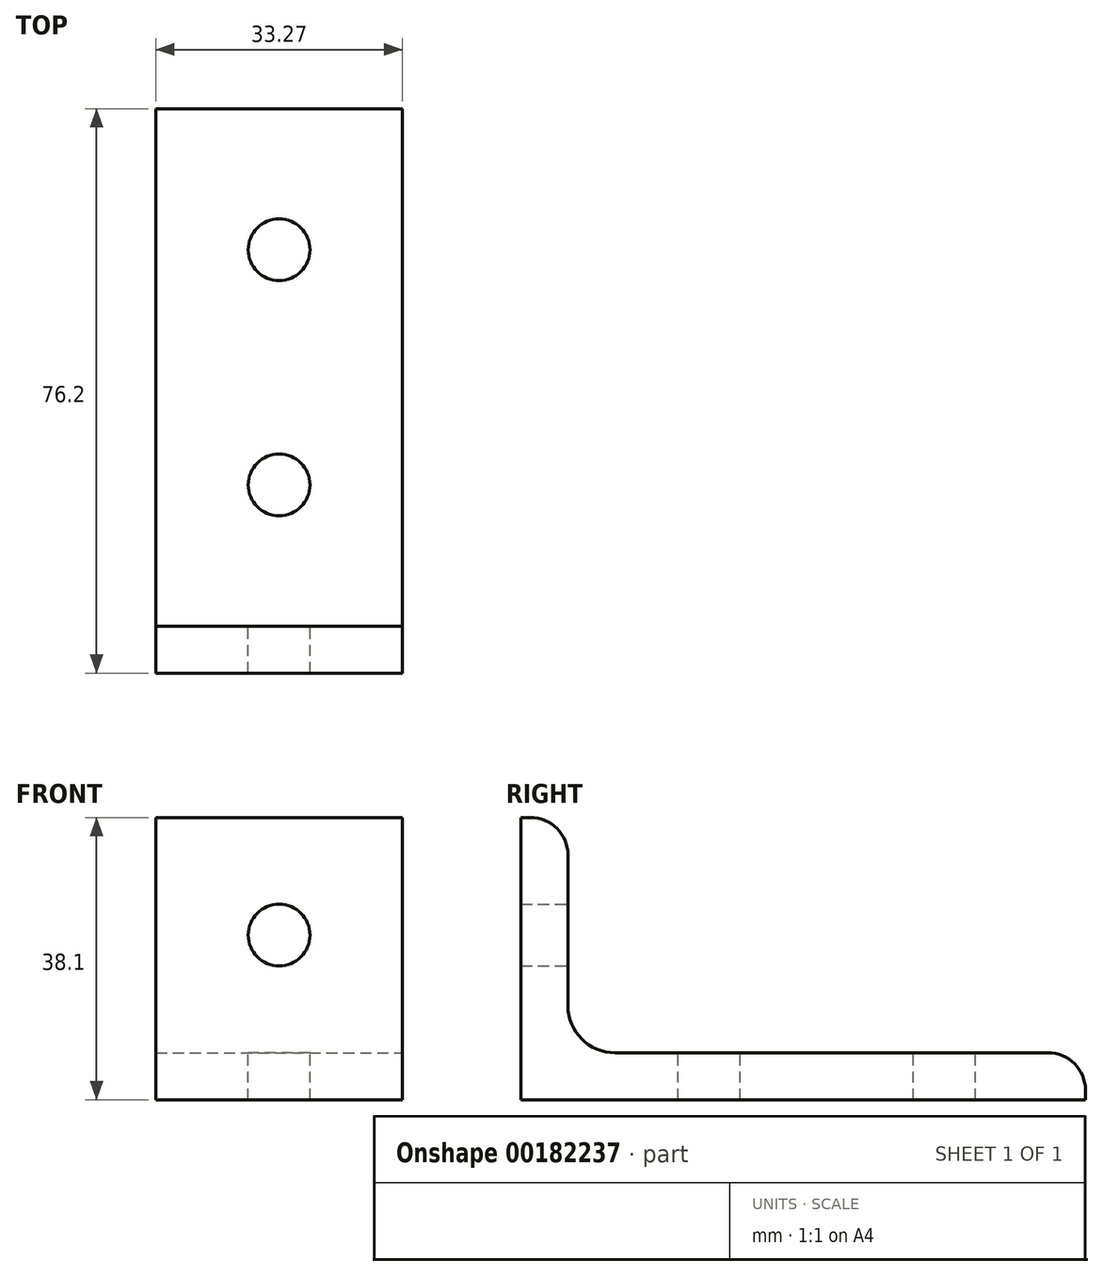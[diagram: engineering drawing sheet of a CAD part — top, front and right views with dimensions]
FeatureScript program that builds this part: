
annotation { "Feature Type Name" : "Feature", "Feature Type Description" : "" }
export const myFeature = defineFeature(function(context is Context, id is Id, definition is map)
    precondition{}
    {
        {
            var Q0;
            Q0=qCreatedBy(makeId("Right.planeOp"),FACE);
            var sketch = newSketch(context, id + "F0", { "sketchPlane" : qUnion([Q0])});
            skLineSegment(sketch, "E0", {"start": v(0, 0) * mm, "end": v(76.2, 0) * mm});
            skLineSegment(sketch, "E1", {"start": v(76.2, 0) * mm, "end": v(76.2, 6.35) * mm});
            skLineSegment(sketch, "E2", {"start": v(76.2, 6.35) * mm, "end": v(6.35, 6.35) * mm});
            skLineSegment(sketch, "E3", {"start": v(6.35, 6.35) * mm, "end": v(6.35, 38.1) * mm});
            skLineSegment(sketch, "E4", {"start": v(6.35, 38.1) * mm, "end": v(0, 38.1) * mm});
            skLineSegment(sketch, "E5", {"start": v(0, 38.1) * mm, "end": v(0, 0) * mm});
            skSolve(sketch);
        }
        {
            var Q0;
            Q0=qSketchRegion(id+"F0",true);
            extrude(context, id + "F1", {"entities" : qUnion([Q0]), "oppositeDirection" : true, "depth" : 33.27 * mm});
        }
        {
            var Q0;
            Q0=makeQuery(id+"F1.opExtrude","SWEPT_EDGE",EDGE,{"disambiguationData":[OSD([sQuery(id+"F0.wireOp",EDGE,"E2"),sQuery(id+"F0.wireOp",EDGE,"E3")])]});
            fillet(context, id + "F2", {"entities" : qUnion([Q0]), "radius" : 6.35 * mm, "tangentPropagation" : true, "allowEdgeOverflow" : false});
        }
        {
            var Q0;
            Q0=makeQuery(id+"F1.opExtrude","SWEPT_EDGE",EDGE,{"disambiguationData":[OSD([sQuery(id+"F0.wireOp",EDGE,"E3"),sQuery(id+"F0.wireOp",EDGE,"E4")])]});
            var Q1;
            Q1=makeQuery(id+"F1.opExtrude","SWEPT_EDGE",EDGE,{"disambiguationData":[OSD([sQuery(id+"F0.wireOp",EDGE,"E1"),sQuery(id+"F0.wireOp",EDGE,"E2")])]});
            fillet(context, id + "F3", {"entities" : qUnion([Q0, Q1]), "radius" : 5.08 * mm, "tangentPropagation" : true, "allowEdgeOverflow" : false});
        }
        {
            var Q0;
            Q0=makeQuery(id+"F1.opExtrude","SWEPT_FACE",FACE,{"disambiguationData":[OSD([sQuery(id+"F0.wireOp",EDGE,"E3")])]});
            var sketch = newSketch(context, id + "F4", { "sketchPlane" : qUnion([Q0])});
            skCircle(sketch, "E6", {"center": v(16.64, 22.23) * mm, "radius": 4.17 * mm});
            skSolve(sketch);
        }
        {
            var Q0;
            Q0=qSketchRegion(id+"F4",true);
            extrude(context, id + "F5", {"entities" : qUnion([Q0]), "operationType" : NewBodyOperationType.REMOVE, "endBound" : BoundingType.THROUGH_ALL, "oppositeDirection" : true, "depth" : 25.4 * mm});
        }
        {
            var Q0;
            Q0=makeQuery(id+"F1.opExtrude","SWEPT_FACE",FACE,{"disambiguationData":[OSD([sQuery(id+"F0.wireOp",EDGE,"E2")])]});
            var sketch = newSketch(context, id + "F6", { "sketchPlane" : qUnion([Q0])});
            skCircle(sketch, "E7", {"center": v(-16.64, 25.4) * mm, "radius": 4.17 * mm});
            skCircle(sketch, "E8", {"center": v(-16.64, 57.15) * mm, "radius": 4.17 * mm});
            skSolve(sketch);
        }
        {
            var Q0;
            Q0=qSketchRegion(id+"F6",true);
            extrude(context, id + "F7", {"entities" : qUnion([Q0]), "operationType" : NewBodyOperationType.REMOVE, "endBound" : BoundingType.THROUGH_ALL, "oppositeDirection" : true, "depth" : 25.4 * mm});
        }
    });
